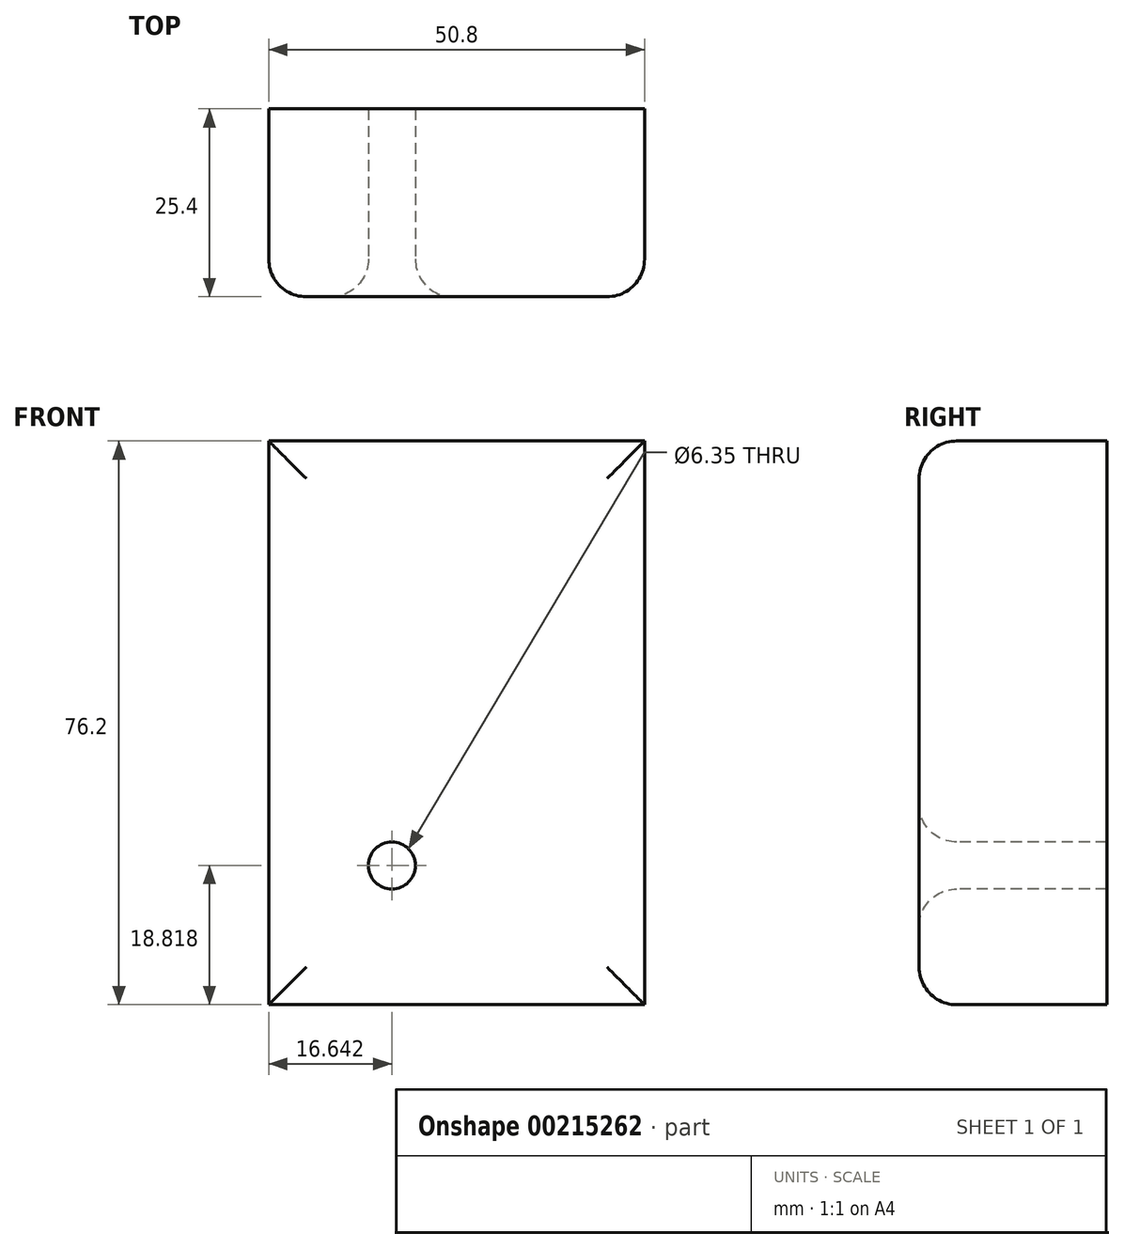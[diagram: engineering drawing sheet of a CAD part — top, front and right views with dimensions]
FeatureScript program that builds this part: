
annotation { "Feature Type Name" : "Feature", "Feature Type Description" : "" }
export const myFeature = defineFeature(function(context is Context, id is Id, definition is map)
    precondition{}
    {
        {
            var Q0;
            Q0=qCreatedBy(makeId("Front.planeOp"),FACE);
            var sketch = newSketch(context, id + "F0", { "sketchPlane" : qUnion([Q0])});
            skLineSegment(sketch, "E0.bottom", {"start": v(0, 0) * mm, "end": v(50.8, 0) * mm});
            skLineSegment(sketch, "E0.top", {"start": v(0, 76.2) * mm, "end": v(50.8, 76.2) * mm});
            skLineSegment(sketch, "E0.left", {"start": v(0, 0) * mm, "end": v(0, 76.2) * mm});
            skLineSegment(sketch, "E0.right", {"start": v(50.8, 0) * mm, "end": v(50.8, 76.2) * mm});
            skSolve(sketch);
        }
        {
            var Q0;
            Q0 = qSketchRegion(id + "F0", true);
            extrude(context, id + "F1", {"entities" : qUnion([Q0]), "depth" : 25.4 * mm});
        }
        {
            var Q0;
            Q0=makeQuery(id+"F1.opExtrude","CAP_FACE",FACE,{"disambiguationData":[OSD([sQuery(id+"F0.wireOp",EDGE,"E0.bottom"),sQuery(id+"F0.wireOp",EDGE,"E0.top"),sQuery(id+"F0.wireOp",EDGE,"E0.left"),sQuery(id+"F0.wireOp",EDGE,"E0.right")])],"isStart":false});
            var sketch = newSketch(context, id + "F2", { "sketchPlane" : qUnion([Q0])});
            skCircle(sketch, "E1", {"center": v(16.64, 18.82) * mm, "radius": 4.72 * mm});
            skSolve(sketch);
        }
        {
            var Q0;
            Q0=sQuery(id+"F2.wireOp",VERTEX,"E1.center");
            var Q1;
            Q1=makeQuery(id+"F1.opExtrude","SWEPT_BODY",BODY,{"disambiguationData":[OSD([sQuery(id+"F0.wireOp",EDGE,"E0.bottom"),sQuery(id+"F0.wireOp",EDGE,"E0.top"),sQuery(id+"F0.wireOp",EDGE,"E0.left"),sQuery(id+"F0.wireOp",EDGE,"E0.right")])]});
            hole(context, id + "F3", {"style" : HoleStyle.SIMPLE, "endStyle" : HoleEndStyle.THROUGH, "holeDiameter" : 6.35 * mm, "locations" : qUnion([Q0]), "scope" : qUnion([Q1]), "isTappedThrough" : true});
        }
        {
            var Q0;
            Q0=makeQuery(id+"F1.opExtrude","CAP_FACE",FACE,{"disambiguationData":[OSD([sQuery(id+"F0.wireOp",EDGE,"E0.bottom"),sQuery(id+"F0.wireOp",EDGE,"E0.top"),sQuery(id+"F0.wireOp",EDGE,"E0.left"),sQuery(id+"F0.wireOp",EDGE,"E0.right")])],"isStart":false});
            fillet(context, id + "F4", {"entities" : qUnion([Q0]), "radius" : 5.08 * mm, "tangentPropagation" : true, "allowEdgeOverflow" : false});
        }
    });
